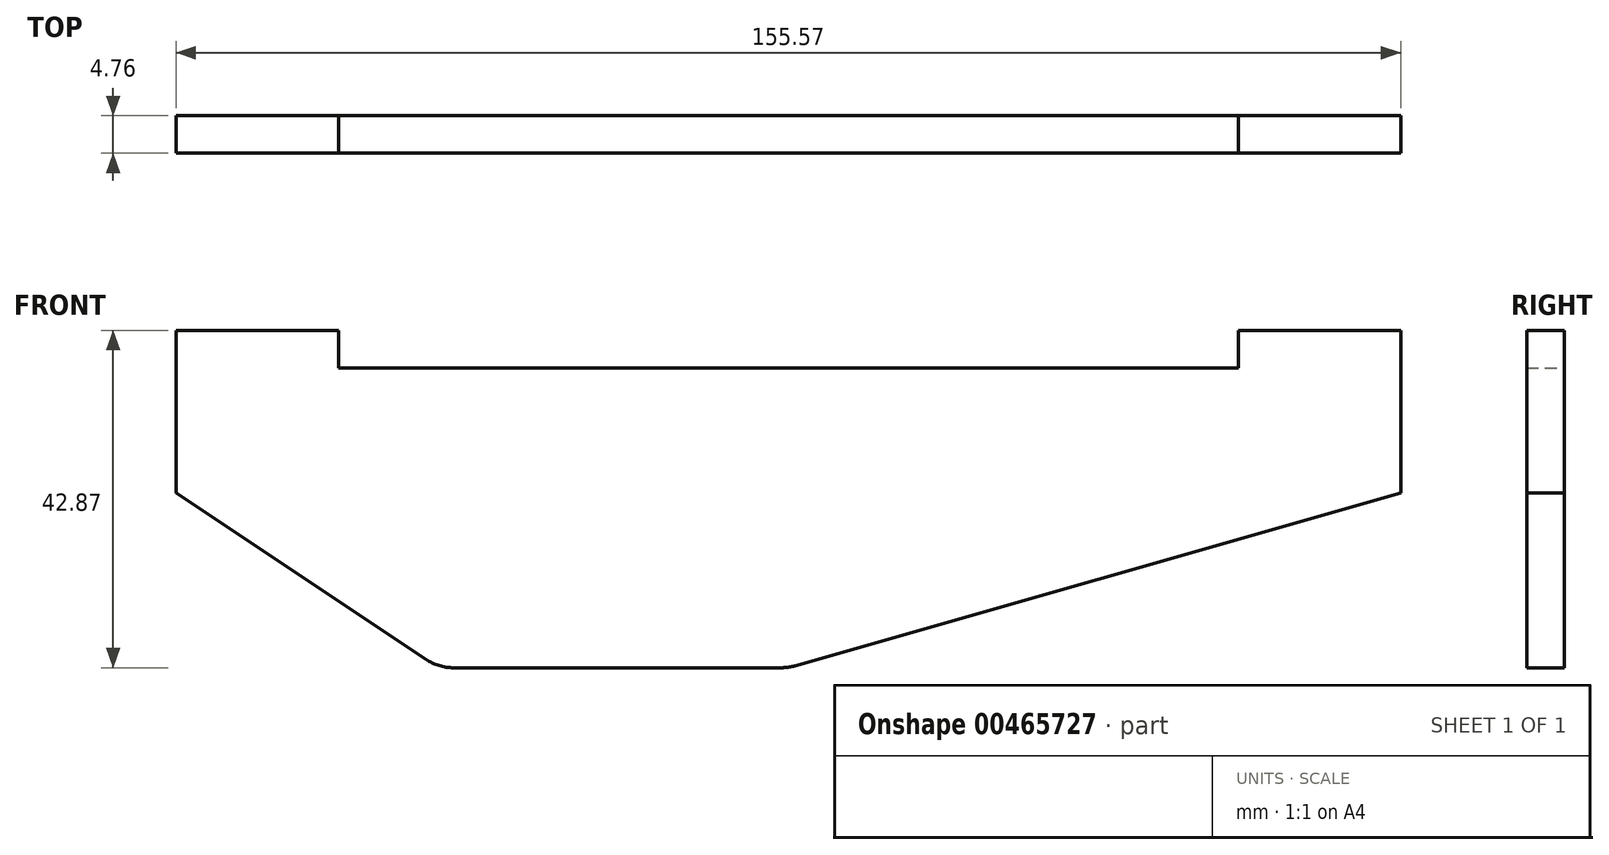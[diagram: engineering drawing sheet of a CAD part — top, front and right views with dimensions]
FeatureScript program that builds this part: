
annotation { "Feature Type Name" : "Feature", "Feature Type Description" : "" }
export const myFeature = defineFeature(function(context is Context, id is Id, definition is map)
    precondition{}
    {
        {
            var Q0;
            Q0=qCreatedBy(makeId("Front.planeOp"),FACE);
            var sketch = newSketch(context, id + "F0", { "sketchPlane" : qUnion([Q0])});
            skLineSegment(sketch, "E0", {"start": v(-65.1, 20.62) * mm, "end": v(-44.47, 20.62) * mm});
            skLineSegment(sketch, "E1", {"start": v(-65.1, 20.62) * mm, "end": v(-65.1, -0.02) * mm});
            skLineSegment(sketch, "E2", {"start": v(-44.47, 20.62) * mm, "end": v(-44.47, 15.85) * mm});
            skLineSegment(sketch, "E3", {"start": v(-44.47, 15.85) * mm, "end": v(69.83, 15.85) * mm});
            skLineSegment(sketch, "E4", {"start": v(69.83, 15.85) * mm, "end": v(69.83, 20.62) * mm});
            skLineSegment(sketch, "E5", {"start": v(69.83, 20.62) * mm, "end": v(90.47, 20.62) * mm});
            skLineSegment(sketch, "E6", {"start": v(90.47, 20.62) * mm, "end": v(90.47, -0.02) * mm});
            skLineSegment(sketch, "E7", {"start": v(-29.84, -22.25) * mm, "end": v(11.8, -22.25) * mm});
            skLineSegment(sketch, "E8", {"start": v(-44.47, 20.62) * mm, "end": v(-44.47, 15.85) * mm, "construction": true});
            skLineSegment(sketch, "E9", {"start": v(-65.1, -0.02) * mm, "end": v(-33.37, -21.18) * mm});
            skLineSegment(sketch, "E10", {"start": v(90.47, -0.02) * mm, "end": v(13.54, -22) * mm});
            skPoint(sketch, "E11.visualSharp", {"position": v(-31.77, -22.25) * mm});
            skArc(sketch, "E11.filletArc", {"start": v(-33.37, -21.18) * mm, "mid": v(-31.68, -21.97) * mm, "end": v(-29.84, -22.25) * mm});
            skPoint(sketch, "E12.visualSharp", {"position": v(12.68, -22.25) * mm});
            skArc(sketch, "E12.filletArc", {"start": v(11.8, -22.25) * mm, "mid": v(12.68, -22.18) * mm, "end": v(13.54, -22) * mm});
            skSolve(sketch);
        }
        {
            var Q0;
            Q0=makeQuery(id+"F0.imprint","IMPRINT",FACE,{"disambiguationData":[TD([[makeQuery(id+"F0.imprint","IMPRINT",EDGE,{"derivedFrom":sQuery(id+"F0.wireOp",EDGE,"E0")}),-1.0]])]});
            extrude(context, id + "F1", {"entities" : qUnion([Q0]), "depth" : 4.76 * mm});
        }
    });
